FCSTD DOCUMENT  (FreeCAD 0.19R24276 (Git))
Label: Z-belt_for_bldc_first_floor_720min
License: All rights reserved
LicenseURL: http://en.wikipedia.org/wiki/All_rights_reserved
objects: Sketcher::SketchObject×1, PartDesign::Body×1
note: 2 computed .brp shape members not serialized (recipe doc carries the construction recipe); baked Part::Feature solids carry a one-line shape summary decoded from their .brp

FEATURE [Sketcher::SketchObject] Sketch
  FullyConstrained = false
  MapMode = 5
  Support = -> [XY_Plane]
  sketch-geometry (23):
    g0: Circle CenterX=0 CenterY=0 CenterZ=0 NormalX=0 NormalY=0 NormalZ=1 AngleXU=0 Radius=30
    g1: Circle CenterX=205 CenterY=0 CenterZ=0 NormalX=0 NormalY=0 NormalZ=1 AngleXU=0 Radius=62.5
    g2: LineSegment StartX=65 StartY=65 StartZ=0 EndX=65 EndY=-65 EndZ=0
    g3: LineSegment StartX=65 StartY=65 StartZ=0 EndX=135 EndY=65 EndZ=0
    g4: LineSegment StartX=135 StartY=65 StartZ=0 EndX=135 EndY=25 EndZ=0
    g5: LineSegment StartX=135 StartY=25 StartZ=0 EndX=65 EndY=25 EndZ=0
    g6: LineSegment StartX=65 StartY=25 StartZ=0 EndX=65 EndY=65 EndZ=0
    g7: LineSegment StartX=0 StartY=0 StartZ=0 EndX=65 EndY=0 EndZ=0
    g8: LineSegment StartX=65 StartY=-65 StartZ=0 EndX=135 EndY=-65 EndZ=0
    g9: LineSegment StartX=135 StartY=-65 StartZ=0 EndX=135 EndY=-25 EndZ=0
    g10: LineSegment StartX=135 StartY=-25 StartZ=0 EndX=65 EndY=-25 EndZ=0
    g11: LineSegment StartX=65 StartY=-25 StartZ=0 EndX=65 EndY=-65 EndZ=0
    g12: Circle CenterX=205 CenterY=0 CenterZ=0 NormalX=0 NormalY=0 NormalZ=1 AngleXU=0 Radius=70
    g13: LineSegment StartX=-4.7561 StartY=29.6206 StartZ=0 EndX=195.091 EndY=61.7096 EndZ=0
    g14: LineSegment StartX=-4.7561 StartY=-29.6206 StartZ=0 EndX=195.091 EndY=-61.7096 EndZ=0
    g15: LineSegment StartX=0 StartY=0 StartZ=0 EndX=-4.7561 EndY=-29.6206 EndZ=0
    g16: LineSegment StartX=0 StartY=0 StartZ=0 EndX=-4.7561 EndY=29.6206 EndZ=0
    g17: LineSegment StartX=205 StartY=0 StartZ=0 EndX=195.091 EndY=61.7096 EndZ=0
    g18: LineSegment StartX=205 StartY=0 StartZ=0 EndX=195.091 EndY=-61.7096 EndZ=0
    g19: LineSegment StartX=205 StartY=0 StartZ=0 EndX=205 EndY=-62.5 EndZ=0
    g20: Circle CenterX=0 CenterY=0 CenterZ=0 NormalX=0 NormalY=0 NormalZ=1 AngleXU=0 Radius=108
    g21: LineSegment StartX=0 StartY=0 StartZ=0 EndX=2e-16 EndY=30.3843 EndZ=0
    g22: LineSegment StartX=205 StartY=0 StartZ=0 EndX=205 EndY=62.5 EndZ=0
  constraints (61):
    c: Coincident(g0,g-1)
    c: PointOnObject(g1,g-1)
    c: Diameter(g0) = 60
    c: Diameter(g1) = 125
    c: Vertical(g2)
    c: DistanceX(g0,g2) = 65
    c: Coincident(g3,g4)
    c: Coincident(g4,g5)
    c: Coincident(g5,g6)
    c: Coincident(g6,g3)
    c: Horizontal(g3)
    c: Horizontal(g5)
    c: Vertical(g4)
    c: Vertical(g6)
    c: Coincident(g3,g2)
    c: Coincident(g7,g0)
    c: PointOnObject(g7,g-1)
    c: Symmetric(g2,g2,g7)
    c: DistanceX(g3,g3) = 70
    c: Coincident(g8,g9)
    c: Coincident(g9,g10)
    c: Coincident(g10,g11)
    c: Coincident(g11,g8)
    c: Horizontal(g10)
    c: Horizontal(g8)
    c: Vertical(g9)
    c: Vertical(g9,g4)
    c: Parallel(g11,g2)
    c: Coincident(g8,g2)
    c: DistanceY(g2,g2) = 130
    c: Coincident(g12,g1)
    c: Diameter(g12) = 140
    c: DistanceY(g5,g2) = 40
    c: DistanceY(g2,g10) = 40
    c: PointOnObject(g13,g0)
    c: PointOnObject(g13,g1)
    c: Tangent(g13,g0)
    c: PointOnObject(g14,g0)
    c: PointOnObject(g14,g1)
    c: Tangent(g14,g1)
    c: Coincident(g15,g0)
    c: DistanceX(g0,g1) = 205
    c: Coincident(g17,g1)
    c: Coincident(g17,g13)
    c: Perpendicular(g17,g13)
    c: Coincident(g18,g1)
    c: Coincident(g18,g14)
    c: Coincident(g14,g15)
    c: Perpendicular(g14,g15)
    c: Coincident(g16,g0)
    c: Coincident(g16,g13)
    c: Coincident(g19,g1)
    c: Vertical(g19)
    c: PointOnObject(g19,g1)
    c: Coincident(g20,g0)
    c: Diameter(g20) = 216
    c: Coincident(g21,g0)
    c: PointOnObject(g21,g13)
    c: Coincident(g22,g1)
    c: Vertical(g22)
    c: PointOnObject(g22,g1)
FEATURE [PartDesign::Body] Body
  Group = -> [Sketch]
  Origin = -> Origin
